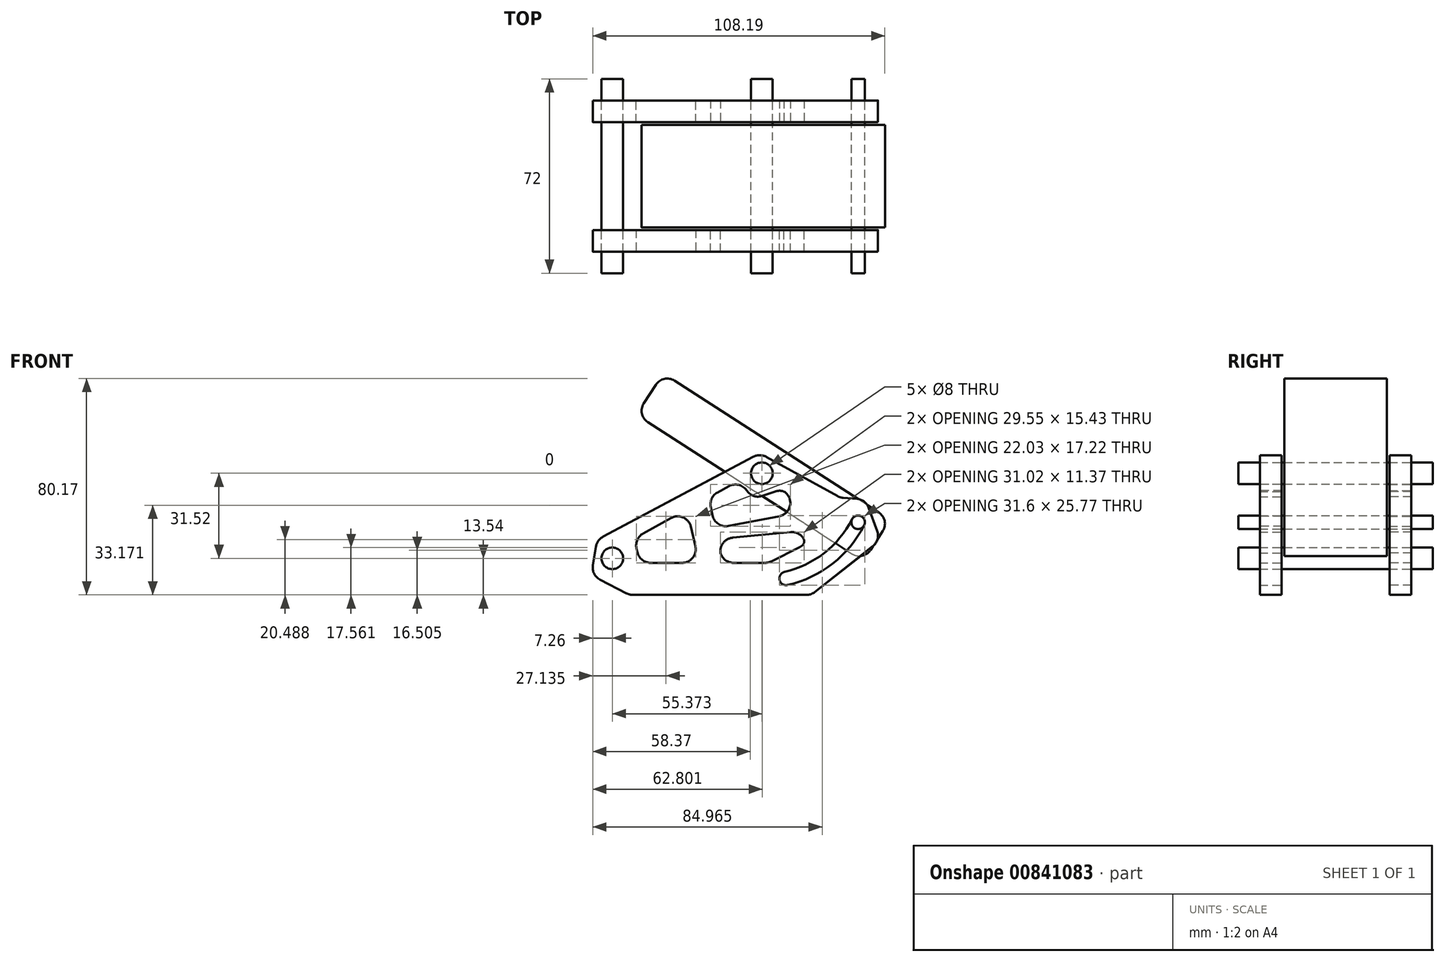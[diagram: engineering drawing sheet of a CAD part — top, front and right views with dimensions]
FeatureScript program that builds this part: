
annotation { "Feature Type Name" : "Feature", "Feature Type Description" : "" }
export const myFeature = defineFeature(function(context is Context, id is Id, definition is map)
    precondition{}
    {
        {
            var Q0;
            Q0=qCreatedBy(makeId("Front.planeOp"),FACE);
            cPlane(context, id + "F0", {"entities" : qUnion([Q0]), "cplaneType" : CPlaneType.OFFSET, "offset" : 20 * mm, "width" : 150 * mm, "height" : 150 * mm});
        }
        {
            var Q0;
            Q0=qCreatedBy(id+"F0.planeOp",FACE);
            var sketch = newSketch(context, id + "F1", { "sketchPlane" : qUnion([Q0])});
            skCircle(sketch, "E0", {"center": v(0, 0) * mm, "radius": 4 * mm});
            skCircle(sketch, "E1", {"center": v(55.37, 31.52) * mm, "radius": 4 * mm});
            skLineSegment(sketch, "E2", {"start": v(80, 0) * mm, "end": v(0, 0) * mm, "construction": true});
            skLineSegment(sketch, "E3", {"start": v(55.37, 31.52) * mm, "end": v(80, 0) * mm, "construction": true});
            skLineSegment(sketch, "E4", {"start": v(55.37, 31.52) * mm, "end": v(91.01, 13.36) * mm, "construction": true});
            skLineSegment(sketch, "E5", {"start": v(55.37, 31.52) * mm, "end": v(64.37, -7.45) * mm, "construction": true});
            skCircle(sketch, "E6", {"center": v(91.01, 13.36) * mm, "radius": 2.5 * mm});
            skCircle(sketch, "E7", {"center": v(64.37, -7.45) * mm, "radius": 2.5 * mm});
            skArc(sketch, "E8", {"start": v(91.01, 13.36) * mm, "mid": v(80, 0) * mm, "end": v(64.37, -7.45) * mm});
            skArc(sketch, "E9", {"start": v(88.79, 14.5) * mm, "mid": v(78.46, 1.97) * mm, "end": v(63.8, -5.02) * mm});
            skArc(sketch, "E10", {"start": v(93.25, 12.24) * mm, "mid": v(81.55, -1.96) * mm, "end": v(64.95, -9.89) * mm});
            skLineSegment(sketch, "E11", {"start": v(54.66, 38.9) * mm, "end": v(-5.6, 6.87) * mm});
            skLineSegment(sketch, "E12", {"start": v(-5.6, 6.87) * mm, "end": v(-7.8, -6.21) * mm});
            skLineSegment(sketch, "E13", {"start": v(-7.8, -6.21) * mm, "end": v(6.38, -13.54) * mm});
            skLineSegment(sketch, "E14", {"start": v(6.38, -13.54) * mm, "end": v(59.78, -13.54) * mm});
            skLineSegment(sketch, "E15", {"start": v(59.78, -13.54) * mm, "end": v(73.66, -13.54) * mm});
            skLineSegment(sketch, "E16", {"start": v(73.66, -13.54) * mm, "end": v(99.31, 6.72) * mm});
            skLineSegment(sketch, "E17", {"start": v(99.31, 6.72) * mm, "end": v(93.82, 21.77) * mm});
            skLineSegment(sketch, "E18", {"start": v(93.82, 21.77) * mm, "end": v(84.36, 22.51) * mm});
            skLineSegment(sketch, "E19", {"start": v(84.36, 22.51) * mm, "end": v(54.66, 38.9) * mm});
            skLineSegment(sketch, "E20", {"start": v(47.08, 28.87) * mm, "end": v(52.1, 21.9) * mm});
            skLineSegment(sketch, "E21", {"start": v(52.1, 21.9) * mm, "end": v(62.24, 25.45) * mm});
            skLineSegment(sketch, "E22", {"start": v(62.24, 25.45) * mm, "end": v(76.65, 18.45) * mm});
            skLineSegment(sketch, "E23", {"start": v(74.1, 10.46) * mm, "end": v(70.6, 4.74) * mm});
            skLineSegment(sketch, "E24", {"start": v(70.6, 4.74) * mm, "end": v(57.72, -1.66) * mm});
            skLineSegment(sketch, "E25", {"start": v(57.72, -1.66) * mm, "end": v(40.83, -1.66) * mm});
            skLineSegment(sketch, "E26", {"start": v(10.22, -1.66) * mm, "end": v(8.13, 7.4) * mm});
            skLineSegment(sketch, "E27", {"start": v(8.13, 7.4) * mm, "end": v(27.6, 18.14) * mm});
            skLineSegment(sketch, "E28", {"start": v(27.6, 18.14) * mm, "end": v(32.18, -1.66) * mm});
            skLineSegment(sketch, "E29", {"start": v(35.67, 22.58) * mm, "end": v(38.12, 11.09) * mm});
            skLineSegment(sketch, "E30", {"start": v(38.12, 11.09) * mm, "end": v(76.65, 18.45) * mm});
            skLineSegment(sketch, "E31", {"start": v(60.54, 9.16) * mm, "end": v(74.1, 10.46) * mm});
            skPoint(sketch, "E31.endSnap0", {"position": v(38.25, 10.46) * mm});
            skLineSegment(sketch, "E32.trimOffspring", {"start": v(35.67, 22.58) * mm, "end": v(47.08, 28.87) * mm});
            skLineSegment(sketch, "E33.trimOffspring", {"start": v(32.18, -1.66) * mm, "end": v(10.22, -1.66) * mm});
            skLineSegment(sketch, "E34.trimOffspring", {"start": v(38.96, 7.1) * mm, "end": v(40.83, -1.66) * mm});
            skLineSegment(sketch, "E35", {"start": v(38.96, 7.1) * mm, "end": v(60.54, 9.16) * mm});
            skSolve(sketch);
        }
        {
            var Q0;
            Q0=makeQuery(id+"F1.imprint","IMPRINT",FACE,{"disambiguationData":[TD([[makeQuery(id+"F1.imprint","IMPRINT",EDGE,{"derivedFrom":sQuery(id+"F1.wireOp",EDGE,"E0")}),-1.0]])]});
            extrude(context, id + "F2", {"entities" : qUnion([Q0]), "depth" : 8 * mm, "offsetDistance" : 25 * mm});
        }
        {
            var Q0;
            Q0=makeQuery(id+"F2.opExtrude","SWEPT_EDGE",EDGE,{"disambiguationData":[OSD([sQuery(id+"F1.wireOp",EDGE,"E11"),sQuery(id+"F1.wireOp",EDGE,"E19")])]});
            var Q1;
            Q1=makeQuery(id+"F2.opExtrude","SWEPT_EDGE",EDGE,{"disambiguationData":[OSD([sQuery(id+"F1.wireOp",EDGE,"E18"),sQuery(id+"F1.wireOp",EDGE,"E19")])]});
            var Q2;
            Q2=makeQuery(id+"F2.opExtrude","SWEPT_EDGE",EDGE,{"disambiguationData":[OSD([sQuery(id+"F1.wireOp",EDGE,"E17"),sQuery(id+"F1.wireOp",EDGE,"E18")])]});
            var Q3;
            Q3=makeQuery(id+"F2.opExtrude","SWEPT_EDGE",EDGE,{"disambiguationData":[OSD([sQuery(id+"F1.wireOp",EDGE,"E16"),sQuery(id+"F1.wireOp",EDGE,"E17")])]});
            var Q4;
            Q4=makeQuery(id+"F2.opExtrude","SWEPT_EDGE",EDGE,{"disambiguationData":[OSD([sQuery(id+"F1.wireOp",EDGE,"E15"),sQuery(id+"F1.wireOp",EDGE,"E16")])]});
            var Q5;
            Q5=makeQuery(id+"F2.opExtrude","SWEPT_EDGE",EDGE,{"disambiguationData":[OSD([sQuery(id+"F1.wireOp",EDGE,"E11"),sQuery(id+"F1.wireOp",EDGE,"E12")])]});
            var Q6;
            Q6=makeQuery(id+"F2.opExtrude","SWEPT_EDGE",EDGE,{"disambiguationData":[OSD([sQuery(id+"F1.wireOp",EDGE,"E12"),sQuery(id+"F1.wireOp",EDGE,"E13")])]});
            var Q7;
            Q7=makeQuery(id+"F2.opExtrude","SWEPT_EDGE",EDGE,{"disambiguationData":[OSD([sQuery(id+"F1.wireOp",EDGE,"E13"),sQuery(id+"F1.wireOp",EDGE,"E14")])]});
            fillet(context, id + "F3", {"entities" : qUnion([Q0, Q1, Q2, Q3, Q4, Q5, Q6, Q7]), "radius" : 5 * mm, "tangentPropagation" : true, "allowEdgeOverflow" : false});
        }
        {
            var Q0;
            Q0=makeQuery(id+"F2.opExtrude","SWEPT_EDGE",EDGE,{"disambiguationData":[OSD([sQuery(id+"F1.wireOp",EDGE,"E26"),sQuery(id+"F1.wireOp",EDGE,"E33.trimOffspring")])]});
            var Q1;
            Q1=makeQuery(id+"F2.opExtrude","SWEPT_EDGE",EDGE,{"disambiguationData":[OSD([sQuery(id+"F1.wireOp",EDGE,"E26"),sQuery(id+"F1.wireOp",EDGE,"E27")])]});
            var Q2;
            Q2=makeQuery(id+"F2.opExtrude","SWEPT_EDGE",EDGE,{"disambiguationData":[OSD([sQuery(id+"F1.wireOp",EDGE,"E27"),sQuery(id+"F1.wireOp",EDGE,"E28")])]});
            var Q3;
            Q3=makeQuery(id+"F2.opExtrude","SWEPT_EDGE",EDGE,{"disambiguationData":[OSD([sQuery(id+"F1.wireOp",EDGE,"E28"),sQuery(id+"F1.wireOp",EDGE,"E33.trimOffspring")])]});
            fillet(context, id + "F4", {"entities" : qUnion([Q0, Q1, Q2, Q3]), "radius" : 5 * mm, "tangentPropagation" : true, "allowEdgeOverflow" : false});
        }
        {
            var Q0;
            Q0=makeQuery(id+"F2.opExtrude","SWEPT_EDGE",EDGE,{"disambiguationData":[OSD([sQuery(id+"F1.wireOp",EDGE,"E29"),sQuery(id+"F1.wireOp",EDGE,"E32.trimOffspring")])]});
            var Q1;
            Q1=makeQuery(id+"F2.opExtrude","SWEPT_EDGE",EDGE,{"disambiguationData":[OSD([sQuery(id+"F1.wireOp",EDGE,"E29"),sQuery(id+"F1.wireOp",EDGE,"E30")])]});
            var Q2;
            Q2=makeQuery(id+"F2.opExtrude","SWEPT_EDGE",EDGE,{"disambiguationData":[OSD([sQuery(id+"F1.wireOp",EDGE,"E22"),sQuery(id+"F1.wireOp",EDGE,"E30")])]});
            var Q3;
            Q3=makeQuery(id+"F2.opExtrude","SWEPT_EDGE",EDGE,{"disambiguationData":[OSD([sQuery(id+"F1.wireOp",EDGE,"E21"),sQuery(id+"F1.wireOp",EDGE,"E22")])]});
            var Q4;
            Q4=makeQuery(id+"F2.opExtrude","SWEPT_EDGE",EDGE,{"disambiguationData":[OSD([sQuery(id+"F1.wireOp",EDGE,"E20"),sQuery(id+"F1.wireOp",EDGE,"E21")])]});
            var Q5;
            Q5=makeQuery(id+"F2.opExtrude","SWEPT_EDGE",EDGE,{"disambiguationData":[OSD([sQuery(id+"F1.wireOp",EDGE,"E20"),sQuery(id+"F1.wireOp",EDGE,"E32.trimOffspring")])]});
            fillet(context, id + "F5", {"entities" : qUnion([Q0, Q1, Q2, Q3, Q4, Q5]), "radius" : 5 * mm, "tangentPropagation" : true, "allowEdgeOverflow" : false});
        }
        {
            var Q0;
            Q0=makeQuery(id+"F2.opExtrude","SWEPT_EDGE",EDGE,{"disambiguationData":[OSD([sQuery(id+"F1.wireOp",EDGE,"E34.trimOffspring"),sQuery(id+"F1.wireOp",EDGE,"E35")])]});
            var Q1;
            Q1=makeQuery(id+"F2.opExtrude","SWEPT_EDGE",EDGE,{"disambiguationData":[OSD([sQuery(id+"F1.wireOp",EDGE,"E25"),sQuery(id+"F1.wireOp",EDGE,"E34.trimOffspring")])]});
            var Q2;
            Q2=makeQuery(id+"F2.opExtrude","SWEPT_EDGE",EDGE,{"disambiguationData":[OSD([sQuery(id+"F1.wireOp",EDGE,"E24"),sQuery(id+"F1.wireOp",EDGE,"E25")])]});
            var Q3;
            Q3=makeQuery(id+"F2.opExtrude","SWEPT_EDGE",EDGE,{"disambiguationData":[OSD([sQuery(id+"F1.wireOp",EDGE,"E23"),sQuery(id+"F1.wireOp",EDGE,"E24")])]});
            fillet(context, id + "F6", {"entities" : qUnion([Q0, Q1, Q2, Q3]), "radius" : 5 * mm, "tangentPropagation" : true, "allowEdgeOverflow" : false});
        }
        {
            var Q0;
            Q0=makeQuery(id+"F2.opExtrude","SWEPT_EDGE",EDGE,{"disambiguationData":[OSD([sQuery(id+"F1.wireOp",EDGE,"E23"),sQuery(id+"F1.wireOp",EDGE,"E31")])]});
            fillet(context, id + "F7", {"entities" : qUnion([Q0]), "radius" : 5 * mm, "tangentPropagation" : true, "allowEdgeOverflow" : false});
        }
        {
            var Q0;
            {var subQ0=sQuery(id+"F1.wireOp",EDGE,"E23");Q0=makeQuery(id+"F7.opFillet","BLEND_EDGE",EDGE,{"blendedFrom":[makeQuery(id+"F2.opExtrude","SWEPT_EDGE",EDGE,{"disambiguationData":[OSD([subQ0,sQuery(id+"F1.wireOp",EDGE,"E31")])]}),makeQuery(id+"F6.opFillet","BLEND_FACE",FACE,{"disambiguationData":[OSD([subQ0,sQuery(id+"F1.wireOp",EDGE,"E24")])]})],"blendedInto":[makeQuery(id+"F6.opFillet","BLEND_FACE",FACE,{"disambiguationData":[OSD([subQ0,sQuery(id+"F1.wireOp",EDGE,"E24")])]})]});}
            fillet(context, id + "F8", {"entities" : qUnion([Q0]), "radius" : 2 * mm, "tangentPropagation" : true, "allowEdgeOverflow" : false});
        }
        {
            var Q0;
            Q0=makeQuery(id+"F2.opExtrude","SWEPT_BODY",BODY,{"disambiguationData":[OSD([sQuery(id+"F1.wireOp",EDGE,"E0"),sQuery(id+"F1.wireOp",EDGE,"E1"),sQuery(id+"F1.wireOp",EDGE,"E6"),sQuery(id+"F1.wireOp",EDGE,"E7"),sQuery(id+"F1.wireOp",EDGE,"E9"),sQuery(id+"F1.wireOp",EDGE,"E10"),sQuery(id+"F1.wireOp",EDGE,"E11"),sQuery(id+"F1.wireOp",EDGE,"E12"),sQuery(id+"F1.wireOp",EDGE,"E13"),sQuery(id+"F1.wireOp",EDGE,"E14"),sQuery(id+"F1.wireOp",EDGE,"E15"),sQuery(id+"F1.wireOp",EDGE,"E16"),sQuery(id+"F1.wireOp",EDGE,"E17"),sQuery(id+"F1.wireOp",EDGE,"E18"),sQuery(id+"F1.wireOp",EDGE,"E19"),sQuery(id+"F1.wireOp",EDGE,"E20"),sQuery(id+"F1.wireOp",EDGE,"E21"),sQuery(id+"F1.wireOp",EDGE,"E22"),sQuery(id+"F1.wireOp",EDGE,"E23"),sQuery(id+"F1.wireOp",EDGE,"E24"),sQuery(id+"F1.wireOp",EDGE,"E25"),sQuery(id+"F1.wireOp",EDGE,"E26"),sQuery(id+"F1.wireOp",EDGE,"E27"),sQuery(id+"F1.wireOp",EDGE,"E28"),sQuery(id+"F1.wireOp",EDGE,"E29"),sQuery(id+"F1.wireOp",EDGE,"E30"),sQuery(id+"F1.wireOp",EDGE,"E31"),sQuery(id+"F1.wireOp",EDGE,"E32.trimOffspring"),sQuery(id+"F1.wireOp",EDGE,"E33.trimOffspring"),sQuery(id+"F1.wireOp",EDGE,"E34.trimOffspring"),sQuery(id+"F1.wireOp",EDGE,"E35")])]});
            var Q1;
            Q1=qCreatedBy(makeId("Front.planeOp"),FACE);
            mirror(context, id + "F9", {"entities" : qUnion([Q0]), "mirrorPlane" : qUnion([Q1])});
        }
        {
            var Q0;
            Q0=qCreatedBy(makeId("Front.planeOp"),FACE);
            var sketch = newSketch(context, id + "F10", { "sketchPlane" : qUnion([Q0])});
            skCircle(sketch, "E36.0", {"center": v(55.37, 31.52) * mm, "radius": 4 * mm});
            skArc(sketch, "E37.0", {"start": v(93.24, 12.22) * mm, "mid": v(92.15, 15.59) * mm, "end": v(88.79, 14.5) * mm});
            skCircle(sketch, "E38", {"center": v(91.01, 13.36) * mm, "radius": 2.5 * mm});
            skLineSegment(sketch, "E39", {"start": v(102.85, 14.29) * mm, "end": v(18.84, 68.54) * mm});
            skLineSegment(sketch, "E40", {"start": v(18.84, 68.54) * mm, "end": v(8.94, 53.2) * mm});
            skLineSegment(sketch, "E41", {"start": v(8.94, 53.2) * mm, "end": v(92.94, -1.05) * mm});
            skLineSegment(sketch, "E42", {"start": v(92.94, -1.05) * mm, "end": v(102.85, 14.29) * mm});
            skSolve(sketch);
        }
        {
            var Q0;
            Q0=makeQuery(id+"F10.imprint","IMPRINT",FACE,{"disambiguationData":[TD([[makeQuery(id+"F10.imprint","IMPRINT",EDGE,{"derivedFrom":sQuery(id+"F10.wireOp",EDGE,"E36.0")}),-1.0]])]});
            extrude(context, id + "F11", {"entities" : qUnion([Q0]), "depth" : 19 * mm, "offsetDistance" : 25 * mm, "hasSecondDirection" : true, "secondDirectionOppositeDirection" : true, "secondDirectionDepth" : 19 * mm});
        }
        {
            var Q0;
            Q0=makeQuery(id+"F11.opExtrude","SWEPT_EDGE",EDGE,{"disambiguationData":[OSD([sQuery(id+"F10.wireOp",EDGE,"E39"),sQuery(id+"F10.wireOp",EDGE,"E42")])]});
            var Q1;
            Q1=makeQuery(id+"F11.opExtrude","SWEPT_EDGE",EDGE,{"disambiguationData":[OSD([sQuery(id+"F10.wireOp",EDGE,"E41"),sQuery(id+"F10.wireOp",EDGE,"E42")])]});
            var Q2;
            Q2=makeQuery(id+"F11.opExtrude","SWEPT_EDGE",EDGE,{"disambiguationData":[OSD([sQuery(id+"F10.wireOp",EDGE,"E39"),sQuery(id+"F10.wireOp",EDGE,"E40")])]});
            var Q3;
            Q3=makeQuery(id+"F11.opExtrude","SWEPT_EDGE",EDGE,{"disambiguationData":[OSD([sQuery(id+"F10.wireOp",EDGE,"E40"),sQuery(id+"F10.wireOp",EDGE,"E41")])]});
            fillet(context, id + "F12", {"entities" : qUnion([Q0, Q1, Q2, Q3]), "radius" : 5 * mm, "tangentPropagation" : true, "allowEdgeOverflow" : false});
        }
        {
            var Q0;
            Q0=qCreatedBy(makeId("Front.planeOp"),FACE);
            var sketch = newSketch(context, id + "F13", { "sketchPlane" : qUnion([Q0])});
            skCircle(sketch, "E43.0", {"center": v(0, 0) * mm, "radius": 4 * mm});
            skCircle(sketch, "E44.0", {"center": v(55.37, 31.52) * mm, "radius": 4 * mm});
            skCircle(sketch, "E45.0", {"center": v(91.01, 13.36) * mm, "radius": 2.5 * mm});
            skSolve(sketch);
        }
        {
            var Q0;
            Q0=makeQuery(id+"F13.imprint","IMPRINT",FACE,{"disambiguationData":[TD([[makeQuery(id+"F13.imprint","IMPRINT",EDGE,{"derivedFrom":sQuery(id+"F13.wireOp",EDGE,"E43.0")}),1.0]])]});
            var Q1;
            Q1=makeQuery(id+"F13.imprint","IMPRINT",FACE,{"disambiguationData":[TD([[makeQuery(id+"F13.imprint","IMPRINT",EDGE,{"derivedFrom":sQuery(id+"F13.wireOp",EDGE,"E44.0")}),1.0]])]});
            var Q2;
            Q2=makeQuery(id+"F13.imprint","IMPRINT",FACE,{"disambiguationData":[TD([[makeQuery(id+"F13.imprint","IMPRINT",EDGE,{"derivedFrom":sQuery(id+"F13.wireOp",EDGE,"E45.0")}),1.0]])]});
            extrude(context, id + "F14", {"entities" : qUnion([Q0, Q1, Q2]), "depth" : 36 * mm, "offsetDistance" : 25 * mm, "hasSecondDirection" : true, "secondDirectionOppositeDirection" : true, "secondDirectionDepth" : 36 * mm});
        }
    });
